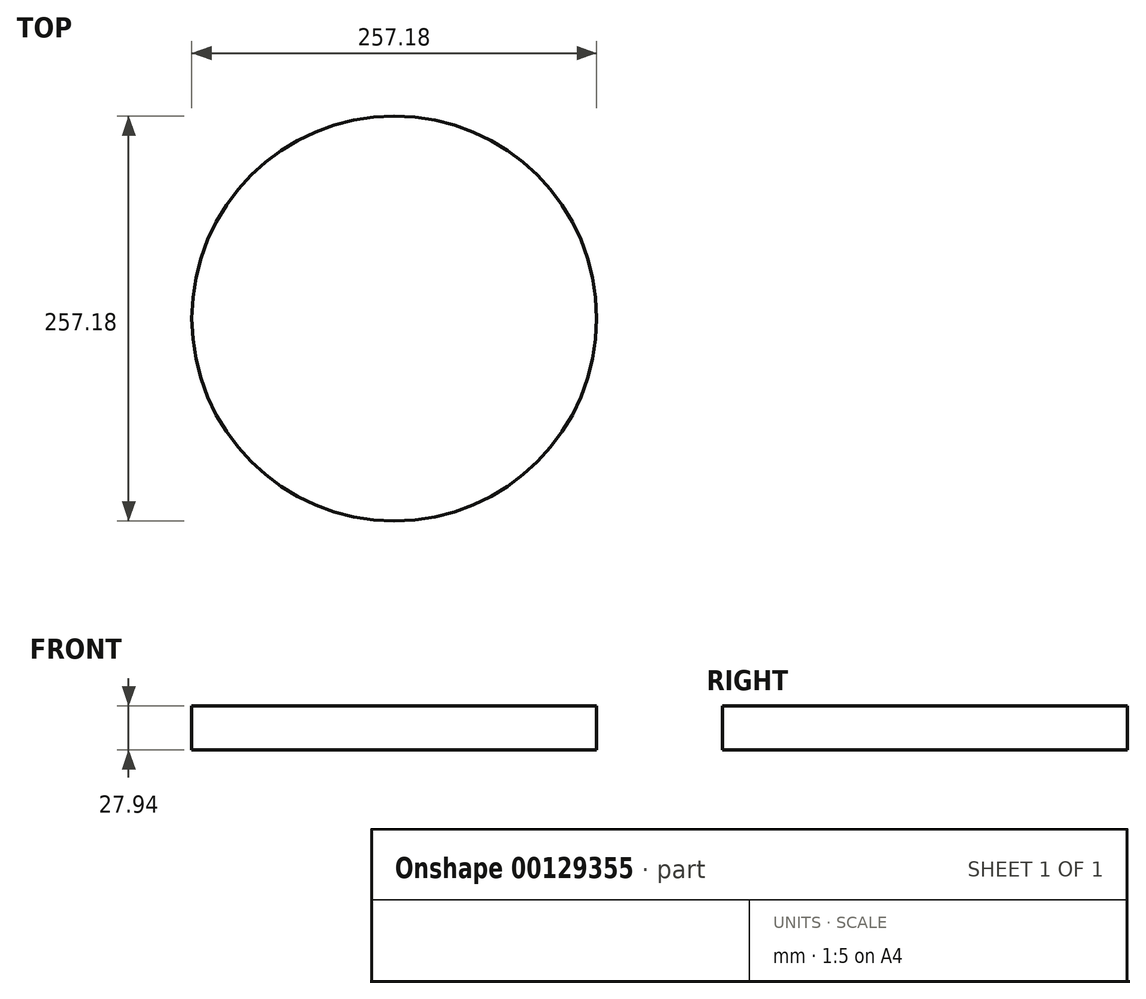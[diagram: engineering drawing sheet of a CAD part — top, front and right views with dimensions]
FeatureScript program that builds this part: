
annotation { "Feature Type Name" : "Feature", "Feature Type Description" : "" }
export const myFeature = defineFeature(function(context is Context, id is Id, definition is map)
    precondition{}
    {
        {
            var Q0;
            Q0=qCreatedBy(makeId("Top.planeOp"),FACE);
            var sketch = newSketch(context, id + "F0", { "sketchPlane" : qUnion([Q0])});
            skCircle(sketch, "E0", {"center": v(0, 0) * mm, "radius": 128.59 * mm});
            skSolve(sketch);
        }
        {
            var Q0;
            Q0 = qSketchRegion(id + "F0", true);
            extrude(context, id + "F1", {"entities" : qUnion([Q0]), "depth" : 27.94 * mm});
        }
    });
